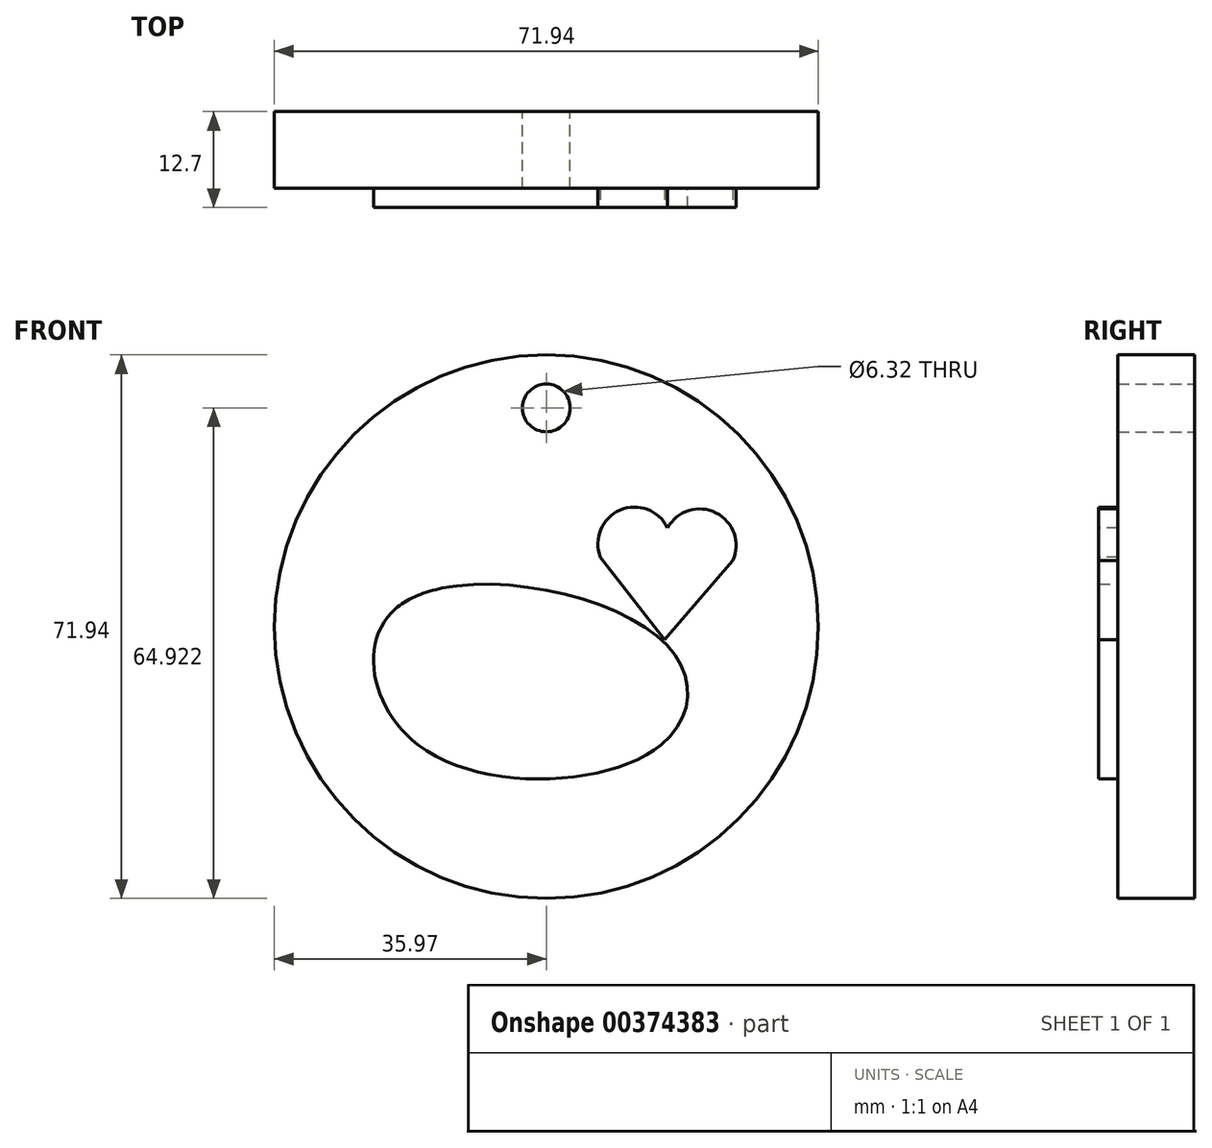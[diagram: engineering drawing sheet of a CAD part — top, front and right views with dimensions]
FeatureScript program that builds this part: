
annotation { "Feature Type Name" : "Feature", "Feature Type Description" : "" }
export const myFeature = defineFeature(function(context is Context, id is Id, definition is map)
    precondition{}
    {
        {
            var Q0;
            Q0=qCreatedBy(makeId("Front.planeOp"),FACE);
            var sketch = newSketch(context, id + "F0", { "sketchPlane" : qUnion([Q0])});
            skCircle(sketch, "E0", {"center": v(0, 0) * mm, "radius": 35.97 * mm});
            skSolve(sketch);
        }
        {
            var Q0;
            Q0 = qSketchRegion(id + "F0", true);
            extrude(context, id + "F1", {"entities" : qUnion([Q0]), "depth" : 12.7 * mm});
        }
        {
            var Q0;
            Q0=makeQuery(id+"F1.opExtrude","CAP_FACE",FACE,{"disambiguationData":[OSD([sQuery(id+"F0.wireOp",EDGE,"E0")])],"isStart":false});
            var sketch = newSketch(context, id + "F2", { "sketchPlane" : qUnion([Q0])});
            skEllipticalArc(sketch, "E1", {});
            skPoint(sketch, "E2.2.internal.snap0", {"position": v(15.22, -15.6) * mm});
            skFitSpline(sketch, "E2", {"points": [v(-17, -15.6) * mm, v(15.22, -15.6) * mm, v(15.22, -1.73) * mm, v(-19.73, 2.56) * mm, v(-17, -15.6) * mm]});
            skArc(sketch, "E3", {"start": v(-17.8, 13.08) * mm, "mid": v(-24.21, 15.07) * mm, "end": v(-26.44, 8.74) * mm});
            skLineSegment(sketch, "E4", {"start": v(-26.44, 8.74) * mm, "end": v(-17.39, -1.73) * mm});
            skArc(sketch, "E5.MirrorCS", {"start": v(-17.8, 13.08) * mm, "mid": v(-11.5, 15.43) * mm, "end": v(-8.93, 9.22) * mm});
            skLineSegment(sketch, "E6.MirrorCS", {"start": v(-8.93, 9.22) * mm, "end": v(-17.39, -1.73) * mm});
            skArc(sketch, "E7.MirrorCS", {"start": v(16.02, 13.08) * mm, "mid": v(22.44, 15.07) * mm, "end": v(24.66, 8.74) * mm});
            skLineSegment(sketch, "E8.MirrorCS", {"start": v(24.66, 8.74) * mm, "end": v(15.61, -1.73) * mm});
            skLineSegment(sketch, "E9.MirrorCS", {"start": v(7.16, 9.22) * mm, "end": v(15.61, -1.73) * mm});
            skArc(sketch, "E10.MirrorCS", {"start": v(16.02, 13.08) * mm, "mid": v(9.73, 15.43) * mm, "end": v(7.16, 9.22) * mm});
            const initialGuessF2  = {"E1": [-0.0008881420638489816, -0.015604647807777988, 1, 0, 0.01610479690134306, 0.012966257095941073, 3.141592653589793, 0]};
            skSetInitialGuess(sketch, initialGuessF2);
            skSolve(sketch);
        }
        {
            var Q0;
            Q0=makeQuery(id+"F2.imprint","IMPRINT",FACE,{"disambiguationData":[TD([[makeQuery(id+"F2.imprint","IMPRINT",EDGE,{"derivedFrom":sQuery(id+"F2.wireOp",EDGE,"E7.MirrorCS")}),-1.0]])]});
            var Q1;
            Q1=makeQuery(id+"F2.imprint","IMPRINT",FACE,{"disambiguationData":[TD([[makeQuery(id+"F2.imprint","IMPRINT",EDGE,{"derivedFrom":sQuery(id+"F2.wireOp",EDGE,"E3")}),1.0]])]});
            var Q2;
            Q2=makeQuery(id+"F2.imprint","IMPRINT",FACE,{"disambiguationData":[TD([[makeQuery(id+"F2.imprint","IMPRINT",EDGE,{"derivedFrom":sQuery(id+"F2.wireOp",EDGE,"E1")}),1.0]])]});
            extrude(context, id + "F3", {"entities" : qUnion([Q0, Q1, Q2]), "operationType" : NewBodyOperationType.REMOVE, "oppositeDirection" : true, "depth" : 2.54 * mm});
        }
        {
            var Q0;
            Q0=qCreatedBy(makeId("Front.planeOp"),FACE);
            var sketch = newSketch(context, id + "F4", { "sketchPlane" : qUnion([Q0])});
            skCircle(sketch, "E11", {"center": v(0, 28.95) * mm, "radius": 3.16 * mm});
            skSolve(sketch);
        }
        {
            var Q0;
            Q0=makeQuery(id+"F4.imprint","IMPRINT",FACE,{"disambiguationData":[TD([[makeQuery(id+"F4.imprint","IMPRINT",EDGE,{"derivedFrom":sQuery(id+"F4.wireOp",EDGE,"E11")}),1.0]])]});
            extrude(context, id + "F5", {"entities" : qUnion([Q0]), "operationType" : NewBodyOperationType.REMOVE, "depth" : 12.7 * mm});
        }
    });
